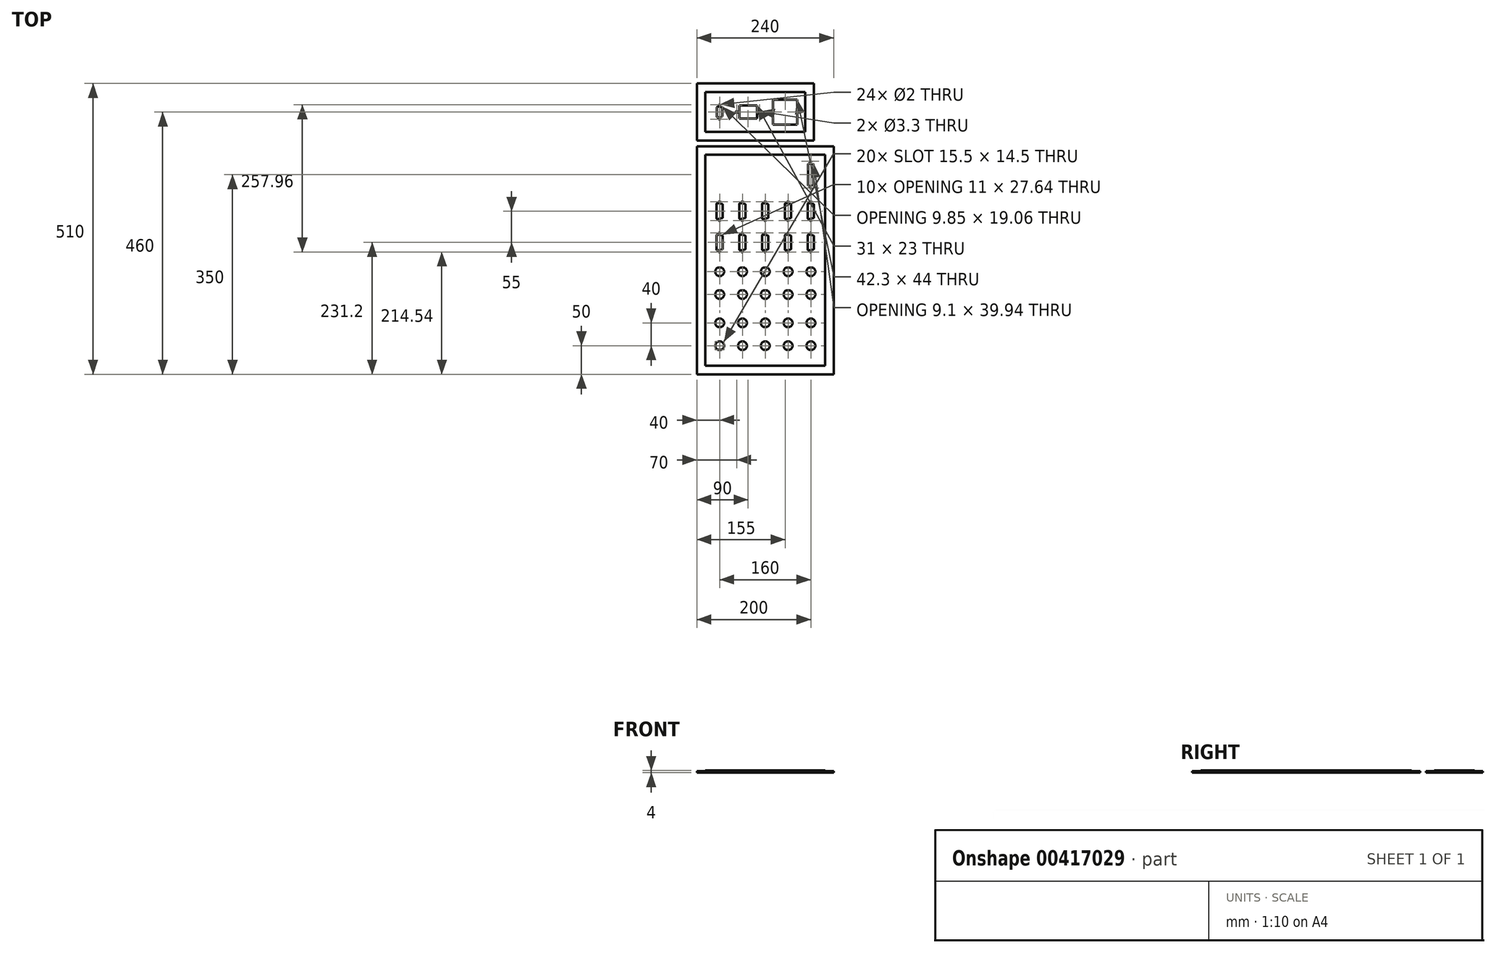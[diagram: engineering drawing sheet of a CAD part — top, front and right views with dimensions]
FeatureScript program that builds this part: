
annotation { "Feature Type Name" : "Feature", "Feature Type Description" : "" }
export const myFeature = defineFeature(function(context is Context, id is Id, definition is map)
    precondition{}
    {
        {
            var Q0;
            Q0=qCreatedBy(makeId("Top.planeOp"),FACE);
            var sketch = newSketch(context, id + "F0", { "sketchPlane" : qUnion([Q0])});
            skLineSegment(sketch, "E0.bottom", {"start": v(-120, -200) * mm, "end": v(120, -200) * mm});
            skLineSegment(sketch, "E0.top", {"start": v(-120, 200) * mm, "end": v(120, 200) * mm});
            skLineSegment(sketch, "E0.left", {"start": v(-120, -200) * mm, "end": v(-120, 200) * mm});
            skLineSegment(sketch, "E0.right", {"start": v(120, -200) * mm, "end": v(120, 200) * mm});
            skArc(sketch, "E1", {"start": v(-82.74, -102.75) * mm, "mid": v(-87.75, -110) * mm, "end": v(-82.74, -117.25) * mm});
            skLineSegment(sketch, "E2", {"start": v(-82.74, -102.75) * mm, "end": v(-77.26, -102.75) * mm});
            skLineSegment(sketch, "E3", {"start": v(-77.26, -117.25) * mm, "end": v(-82.74, -117.25) * mm});
            skLineSegment(sketch, "E4", {"start": v(-80, -110) * mm, "end": v(-87.75, -110) * mm, "construction": true});
            skArc(sketch, "E5.trimOffspring", {"start": v(-77.26, -117.25) * mm, "mid": v(-72.25, -110) * mm, "end": v(-77.26, -102.75) * mm});
            skLineSegment(sketch, "E6.0.1.0", {"start": v(-77.26, -157.25) * mm, "end": v(-82.74, -157.25) * mm});
            skLineSegment(sketch, "E6.0.1.1", {"start": v(-82.74, -142.75) * mm, "end": v(-77.26, -142.75) * mm});
            skArc(sketch, "E6.0.1.2", {"start": v(-82.74, -142.75) * mm, "mid": v(-87.75, -150) * mm, "end": v(-82.74, -157.25) * mm});
            skLineSegment(sketch, "E6.0.1.3", {"start": v(-80, -150) * mm, "end": v(-87.75, -150) * mm, "construction": true});
            skArc(sketch, "E6.0.1.4", {"start": v(-77.26, -157.25) * mm, "mid": v(-72.25, -150) * mm, "end": v(-77.26, -142.75) * mm});
            skLineSegment(sketch, "E6.direction1", {"start": v(-82.74, -117.25) * mm, "end": v(-42.74, -117.25) * mm, "construction": true});
            skLineSegment(sketch, "E6.direction2", {"start": v(-82.74, -117.25) * mm, "end": v(-82.74, -157.25) * mm, "construction": true});
            skLineSegment(sketch, "E7.0.1.0", {"start": v(-37.26, -117.25) * mm, "end": v(-42.74, -117.25) * mm});
            skLineSegment(sketch, "E7.3.1.0", {"start": v(-42.74, -102.75) * mm, "end": v(-37.26, -102.75) * mm});
            skArc(sketch, "E7.6.1.0", {"start": v(-42.74, -102.75) * mm, "mid": v(-47.75, -110) * mm, "end": v(-42.74, -117.25) * mm});
            skLineSegment(sketch, "E7.10.1.0", {"start": v(-40, -110) * mm, "end": v(-47.75, -110) * mm, "construction": true});
            skArc(sketch, "E7.13.1.0", {"start": v(-37.26, -117.25) * mm, "mid": v(-32.25, -110) * mm, "end": v(-37.26, -102.75) * mm});
            skLineSegment(sketch, "E7.0.1.1", {"start": v(-37.26, -157.25) * mm, "end": v(-42.74, -157.25) * mm});
            skLineSegment(sketch, "E7.3.1.1", {"start": v(-42.74, -142.75) * mm, "end": v(-37.26, -142.75) * mm});
            skArc(sketch, "E7.6.1.1", {"start": v(-42.74, -142.75) * mm, "mid": v(-47.75, -150) * mm, "end": v(-42.74, -157.25) * mm});
            skLineSegment(sketch, "E7.10.1.1", {"start": v(-40, -150) * mm, "end": v(-47.75, -150) * mm, "construction": true});
            skArc(sketch, "E7.13.1.1", {"start": v(-37.26, -157.25) * mm, "mid": v(-32.25, -150) * mm, "end": v(-37.26, -142.75) * mm});
            skLineSegment(sketch, "E7.0.2.0", {"start": v(2.74, -117.25) * mm, "end": v(-2.74, -117.25) * mm});
            skLineSegment(sketch, "E7.3.2.0", {"start": v(-2.74, -102.75) * mm, "end": v(2.74, -102.75) * mm});
            skArc(sketch, "E7.6.2.0", {"start": v(-2.74, -102.75) * mm, "mid": v(-7.75, -110) * mm, "end": v(-2.74, -117.25) * mm});
            skLineSegment(sketch, "E7.10.2.0", {"start": v(0, -110) * mm, "end": v(-7.75, -110) * mm, "construction": true});
            skArc(sketch, "E7.13.2.0", {"start": v(2.74, -117.25) * mm, "mid": v(7.75, -110) * mm, "end": v(2.74, -102.75) * mm});
            skLineSegment(sketch, "E7.0.2.1", {"start": v(2.74, -157.25) * mm, "end": v(-2.74, -157.25) * mm});
            skLineSegment(sketch, "E7.3.2.1", {"start": v(-2.74, -142.75) * mm, "end": v(2.74, -142.75) * mm});
            skArc(sketch, "E7.6.2.1", {"start": v(-2.74, -142.75) * mm, "mid": v(-7.75, -150) * mm, "end": v(-2.74, -157.25) * mm});
            skLineSegment(sketch, "E7.10.2.1", {"start": v(0, -150) * mm, "end": v(-7.75, -150) * mm, "construction": true});
            skArc(sketch, "E7.13.2.1", {"start": v(2.74, -157.25) * mm, "mid": v(7.75, -150) * mm, "end": v(2.74, -142.75) * mm});
            skLineSegment(sketch, "E7.0.3.0", {"start": v(42.74, -117.25) * mm, "end": v(37.26, -117.25) * mm});
            skLineSegment(sketch, "E7.3.3.0", {"start": v(37.26, -102.75) * mm, "end": v(42.74, -102.75) * mm});
            skArc(sketch, "E7.6.3.0", {"start": v(37.26, -102.75) * mm, "mid": v(32.25, -110) * mm, "end": v(37.26, -117.25) * mm});
            skLineSegment(sketch, "E7.10.3.0", {"start": v(40, -110) * mm, "end": v(32.25, -110) * mm, "construction": true});
            skArc(sketch, "E7.13.3.0", {"start": v(42.74, -117.25) * mm, "mid": v(47.75, -110) * mm, "end": v(42.74, -102.75) * mm});
            skLineSegment(sketch, "E7.0.3.1", {"start": v(42.74, -157.25) * mm, "end": v(37.26, -157.25) * mm});
            skLineSegment(sketch, "E7.3.3.1", {"start": v(37.26, -142.75) * mm, "end": v(42.74, -142.75) * mm});
            skArc(sketch, "E7.6.3.1", {"start": v(37.26, -142.75) * mm, "mid": v(32.25, -150) * mm, "end": v(37.26, -157.25) * mm});
            skLineSegment(sketch, "E7.10.3.1", {"start": v(40, -150) * mm, "end": v(32.25, -150) * mm, "construction": true});
            skArc(sketch, "E7.13.3.1", {"start": v(42.74, -157.25) * mm, "mid": v(47.75, -150) * mm, "end": v(42.74, -142.75) * mm});
            skLineSegment(sketch, "E7.0.4.0", {"start": v(82.74, -117.25) * mm, "end": v(77.26, -117.25) * mm});
            skLineSegment(sketch, "E7.3.4.0", {"start": v(77.26, -102.75) * mm, "end": v(82.74, -102.75) * mm});
            skArc(sketch, "E7.6.4.0", {"start": v(77.26, -102.75) * mm, "mid": v(72.25, -110) * mm, "end": v(77.26, -117.25) * mm});
            skLineSegment(sketch, "E7.10.4.0", {"start": v(80, -110) * mm, "end": v(72.25, -110) * mm, "construction": true});
            skArc(sketch, "E7.13.4.0", {"start": v(82.74, -117.25) * mm, "mid": v(87.75, -110) * mm, "end": v(82.74, -102.75) * mm});
            skLineSegment(sketch, "E7.0.4.1", {"start": v(82.74, -157.25) * mm, "end": v(77.26, -157.25) * mm});
            skLineSegment(sketch, "E7.3.4.1", {"start": v(77.26, -142.75) * mm, "end": v(82.74, -142.75) * mm});
            skArc(sketch, "E7.6.4.1", {"start": v(77.26, -142.75) * mm, "mid": v(72.25, -150) * mm, "end": v(77.26, -157.25) * mm});
            skLineSegment(sketch, "E7.10.4.1", {"start": v(80, -150) * mm, "end": v(72.25, -150) * mm, "construction": true});
            skArc(sketch, "E7.13.4.1", {"start": v(82.74, -157.25) * mm, "mid": v(87.75, -150) * mm, "end": v(82.74, -142.75) * mm});
            skLineSegment(sketch, "E8.bottom", {"start": v(-105, 185) * mm, "end": v(105, 185) * mm, "construction": true});
            skLineSegment(sketch, "E8.top", {"start": v(-105, -185) * mm, "end": v(105, -185) * mm, "construction": true});
            skLineSegment(sketch, "E8.left", {"start": v(-105, 185) * mm, "end": v(-105, -185) * mm, "construction": true});
            skLineSegment(sketch, "E8.right", {"start": v(105, 185) * mm, "end": v(105, -185) * mm, "construction": true});
            skArc(sketch, "E9", {"start": v(-82.74, -12.75) * mm, "mid": v(-87.75, -20) * mm, "end": v(-82.74, -27.25) * mm});
            skLineSegment(sketch, "E10", {"start": v(-82.74, -12.75) * mm, "end": v(-77.26, -12.75) * mm});
            skLineSegment(sketch, "E11", {"start": v(-77.26, -27.25) * mm, "end": v(-82.74, -27.25) * mm});
            skLineSegment(sketch, "E12", {"start": v(-80, -20) * mm, "end": v(-87.75, -20) * mm, "construction": true});
            skArc(sketch, "E13.trimOffspring", {"start": v(-77.26, -27.25) * mm, "mid": v(-72.25, -20) * mm, "end": v(-77.26, -12.75) * mm});
            skLineSegment(sketch, "E14", {"start": v(-83.74, 100) * mm, "end": v(-75.74, 98.59) * mm});
            skLineSegment(sketch, "E15", {"start": v(-74.5, 97.11) * mm, "end": v(-74.5, 75.29) * mm});
            skLineSegment(sketch, "E16", {"start": v(-75.74, 73.81) * mm, "end": v(-83.74, 72.4) * mm});
            skLineSegment(sketch, "E17", {"start": v(-85.5, 73.88) * mm, "end": v(-85.5, 98.52) * mm});
            skLineSegment(sketch, "E18", {"start": v(-80, 99.34) * mm, "end": v(-80, 73.06) * mm, "construction": true});
            skPoint(sketch, "E19.visualSharp", {"position": v(-85.5, 100.31) * mm});
            skArc(sketch, "E19.filletArc", {"start": v(-83.74, 100) * mm, "mid": v(-84.96, 99.67) * mm, "end": v(-85.5, 98.52) * mm});
            skPoint(sketch, "E20.visualSharp", {"position": v(-74.5, 98.37) * mm});
            skArc(sketch, "E20.filletArc", {"start": v(-74.5, 97.11) * mm, "mid": v(-74.85, 98.08) * mm, "end": v(-75.74, 98.59) * mm});
            skPoint(sketch, "E21.visualSharp", {"position": v(-74.5, 74.03) * mm});
            skArc(sketch, "E21.filletArc", {"start": v(-75.74, 73.81) * mm, "mid": v(-74.85, 74.32) * mm, "end": v(-74.5, 75.29) * mm});
            skPoint(sketch, "E22.visualSharp", {"position": v(-85.5, 72.09) * mm});
            skArc(sketch, "E22.filletArc", {"start": v(-85.5, 73.88) * mm, "mid": v(-84.96, 72.73) * mm, "end": v(-83.74, 72.4) * mm});
            skCircle(sketch, "E23", {"center": v(-80, 102.86) * mm, "radius": 1 * mm});
            skCircle(sketch, "E24", {"center": v(-80, 69.54) * mm, "radius": 1 * mm});
            skLineSegment(sketch, "E25", {"start": v(-84, 86.2) * mm, "end": v(-76.01, 86.2) * mm, "construction": true});
            skPoint(sketch, "E26.0.1.0", {"position": v(-85.5, 45.31) * mm});
            skPoint(sketch, "E26.0.1.1", {"position": v(-85.5, 17.09) * mm});
            skPoint(sketch, "E26.0.1.2", {"position": v(-74.5, 43.37) * mm});
            skLineSegment(sketch, "E26.0.1.3", {"start": v(-80, 44.34) * mm, "end": v(-80, 18.06) * mm, "construction": true});
            skLineSegment(sketch, "E26.0.1.4", {"start": v(-84, 31.2) * mm, "end": v(-76.01, 31.2) * mm, "construction": true});
            skPoint(sketch, "E26.0.1.5", {"position": v(-74.5, 19.03) * mm});
            skLineSegment(sketch, "E26.0.1.6", {"start": v(-74.5, 42.11) * mm, "end": v(-74.5, 20.29) * mm});
            skLineSegment(sketch, "E26.0.1.7", {"start": v(-85.5, 18.88) * mm, "end": v(-85.5, 43.52) * mm});
            skCircle(sketch, "E26.0.1.8", {"center": v(-80, 47.86) * mm, "radius": 1 * mm});
            skLineSegment(sketch, "E26.0.1.9", {"start": v(-83.74, 45) * mm, "end": v(-75.74, 43.59) * mm});
            skCircle(sketch, "E26.0.1.10", {"center": v(-80, 14.54) * mm, "radius": 1 * mm});
            skArc(sketch, "E26.0.1.11", {"start": v(-83.74, 45) * mm, "mid": v(-84.96, 44.67) * mm, "end": v(-85.5, 43.52) * mm});
            skArc(sketch, "E26.0.1.12", {"start": v(-85.5, 18.88) * mm, "mid": v(-84.96, 17.73) * mm, "end": v(-83.74, 17.4) * mm});
            skLineSegment(sketch, "E26.0.1.13", {"start": v(-75.74, 18.81) * mm, "end": v(-83.74, 17.4) * mm});
            skArc(sketch, "E26.0.1.14", {"start": v(-75.74, 18.81) * mm, "mid": v(-74.85, 19.32) * mm, "end": v(-74.5, 20.29) * mm});
            skArc(sketch, "E26.0.1.15", {"start": v(-74.5, 42.11) * mm, "mid": v(-74.85, 43.08) * mm, "end": v(-75.74, 43.59) * mm});
            skPoint(sketch, "E26.1.0.0", {"position": v(-45.5, 100.31) * mm});
            skPoint(sketch, "E26.1.0.1", {"position": v(-45.5, 72.09) * mm});
            skPoint(sketch, "E26.1.0.2", {"position": v(-34.5, 98.37) * mm});
            skLineSegment(sketch, "E26.1.0.3", {"start": v(-40, 99.34) * mm, "end": v(-40, 73.06) * mm, "construction": true});
            skLineSegment(sketch, "E26.1.0.4", {"start": v(-44, 86.2) * mm, "end": v(-36.01, 86.2) * mm, "construction": true});
            skPoint(sketch, "E26.1.0.5", {"position": v(-34.5, 74.03) * mm});
            skLineSegment(sketch, "E26.1.0.6", {"start": v(-34.5, 97.11) * mm, "end": v(-34.5, 75.29) * mm});
            skLineSegment(sketch, "E26.1.0.7", {"start": v(-45.5, 73.88) * mm, "end": v(-45.5, 98.52) * mm});
            skCircle(sketch, "E26.1.0.8", {"center": v(-40, 102.86) * mm, "radius": 1 * mm});
            skLineSegment(sketch, "E26.1.0.9", {"start": v(-43.74, 100) * mm, "end": v(-35.74, 98.59) * mm});
            skCircle(sketch, "E26.1.0.10", {"center": v(-40, 69.54) * mm, "radius": 1 * mm});
            skArc(sketch, "E26.1.0.11", {"start": v(-43.74, 100) * mm, "mid": v(-44.96, 99.67) * mm, "end": v(-45.5, 98.52) * mm});
            skArc(sketch, "E26.1.0.12", {"start": v(-45.5, 73.88) * mm, "mid": v(-44.96, 72.73) * mm, "end": v(-43.74, 72.4) * mm});
            skLineSegment(sketch, "E26.1.0.13", {"start": v(-35.74, 73.81) * mm, "end": v(-43.74, 72.4) * mm});
            skArc(sketch, "E26.1.0.14", {"start": v(-35.74, 73.81) * mm, "mid": v(-34.85, 74.32) * mm, "end": v(-34.5, 75.29) * mm});
            skArc(sketch, "E26.1.0.15", {"start": v(-34.5, 97.11) * mm, "mid": v(-34.85, 98.08) * mm, "end": v(-35.74, 98.59) * mm});
            skPoint(sketch, "E26.1.1.0", {"position": v(-45.5, 45.31) * mm});
            skPoint(sketch, "E26.1.1.1", {"position": v(-45.5, 17.09) * mm});
            skPoint(sketch, "E26.1.1.2", {"position": v(-34.5, 43.37) * mm});
            skLineSegment(sketch, "E26.1.1.3", {"start": v(-40, 44.34) * mm, "end": v(-40, 18.06) * mm, "construction": true});
            skLineSegment(sketch, "E26.1.1.4", {"start": v(-44, 31.2) * mm, "end": v(-36.01, 31.2) * mm, "construction": true});
            skPoint(sketch, "E26.1.1.5", {"position": v(-34.5, 19.03) * mm});
            skLineSegment(sketch, "E26.1.1.6", {"start": v(-34.5, 42.11) * mm, "end": v(-34.5, 20.29) * mm});
            skLineSegment(sketch, "E26.1.1.7", {"start": v(-45.5, 18.88) * mm, "end": v(-45.5, 43.52) * mm});
            skCircle(sketch, "E26.1.1.8", {"center": v(-40, 47.86) * mm, "radius": 1 * mm});
            skLineSegment(sketch, "E26.1.1.9", {"start": v(-43.74, 45) * mm, "end": v(-35.74, 43.59) * mm});
            skCircle(sketch, "E26.1.1.10", {"center": v(-40, 14.54) * mm, "radius": 1 * mm});
            skArc(sketch, "E26.1.1.11", {"start": v(-43.74, 45) * mm, "mid": v(-44.96, 44.67) * mm, "end": v(-45.5, 43.52) * mm});
            skArc(sketch, "E26.1.1.12", {"start": v(-45.5, 18.88) * mm, "mid": v(-44.96, 17.73) * mm, "end": v(-43.74, 17.4) * mm});
            skLineSegment(sketch, "E26.1.1.13", {"start": v(-35.74, 18.81) * mm, "end": v(-43.74, 17.4) * mm});
            skArc(sketch, "E26.1.1.14", {"start": v(-35.74, 18.81) * mm, "mid": v(-34.85, 19.32) * mm, "end": v(-34.5, 20.29) * mm});
            skArc(sketch, "E26.1.1.15", {"start": v(-34.5, 42.11) * mm, "mid": v(-34.85, 43.08) * mm, "end": v(-35.74, 43.59) * mm});
            skPoint(sketch, "E26.2.0.0", {"position": v(-5.5, 100.31) * mm});
            skPoint(sketch, "E26.2.0.1", {"position": v(-5.5, 72.09) * mm});
            skPoint(sketch, "E26.2.0.2", {"position": v(5.5, 98.37) * mm});
            skLineSegment(sketch, "E26.2.0.3", {"start": v(0, 99.34) * mm, "end": v(0, 73.06) * mm, "construction": true});
            skLineSegment(sketch, "E26.2.0.4", {"start": v(-4, 86.2) * mm, "end": v(3.99, 86.2) * mm, "construction": true});
            skPoint(sketch, "E26.2.0.5", {"position": v(5.5, 74.03) * mm});
            skLineSegment(sketch, "E26.2.0.6", {"start": v(5.5, 97.11) * mm, "end": v(5.5, 75.29) * mm});
            skLineSegment(sketch, "E26.2.0.7", {"start": v(-5.5, 73.88) * mm, "end": v(-5.5, 98.52) * mm});
            skCircle(sketch, "E26.2.0.8", {"center": v(0, 102.86) * mm, "radius": 1 * mm});
            skLineSegment(sketch, "E26.2.0.9", {"start": v(-3.74, 100) * mm, "end": v(4.26, 98.59) * mm});
            skCircle(sketch, "E26.2.0.10", {"center": v(0, 69.54) * mm, "radius": 1 * mm});
            skArc(sketch, "E26.2.0.11", {"start": v(-3.74, 100) * mm, "mid": v(-4.96, 99.67) * mm, "end": v(-5.5, 98.52) * mm});
            skArc(sketch, "E26.2.0.12", {"start": v(-5.5, 73.88) * mm, "mid": v(-4.96, 72.73) * mm, "end": v(-3.74, 72.4) * mm});
            skLineSegment(sketch, "E26.2.0.13", {"start": v(4.26, 73.81) * mm, "end": v(-3.74, 72.4) * mm});
            skArc(sketch, "E26.2.0.14", {"start": v(4.26, 73.81) * mm, "mid": v(5.15, 74.32) * mm, "end": v(5.5, 75.29) * mm});
            skArc(sketch, "E26.2.0.15", {"start": v(5.5, 97.11) * mm, "mid": v(5.15, 98.08) * mm, "end": v(4.26, 98.59) * mm});
            skPoint(sketch, "E26.2.1.0", {"position": v(-5.5, 45.31) * mm});
            skPoint(sketch, "E26.2.1.1", {"position": v(-5.5, 17.09) * mm});
            skPoint(sketch, "E26.2.1.2", {"position": v(5.5, 43.37) * mm});
            skLineSegment(sketch, "E26.2.1.3", {"start": v(0, 44.34) * mm, "end": v(0, 18.06) * mm, "construction": true});
            skLineSegment(sketch, "E26.2.1.4", {"start": v(-4, 31.2) * mm, "end": v(3.99, 31.2) * mm, "construction": true});
            skPoint(sketch, "E26.2.1.5", {"position": v(5.5, 19.03) * mm});
            skLineSegment(sketch, "E26.2.1.6", {"start": v(5.5, 42.11) * mm, "end": v(5.5, 20.29) * mm});
            skLineSegment(sketch, "E26.2.1.7", {"start": v(-5.5, 18.88) * mm, "end": v(-5.5, 43.52) * mm});
            skCircle(sketch, "E26.2.1.8", {"center": v(0, 47.86) * mm, "radius": 1 * mm});
            skLineSegment(sketch, "E26.2.1.9", {"start": v(-3.74, 45) * mm, "end": v(4.26, 43.59) * mm});
            skCircle(sketch, "E26.2.1.10", {"center": v(0, 14.54) * mm, "radius": 1 * mm});
            skArc(sketch, "E26.2.1.11", {"start": v(-3.74, 45) * mm, "mid": v(-4.96, 44.67) * mm, "end": v(-5.5, 43.52) * mm});
            skArc(sketch, "E26.2.1.12", {"start": v(-5.5, 18.88) * mm, "mid": v(-4.96, 17.73) * mm, "end": v(-3.74, 17.4) * mm});
            skLineSegment(sketch, "E26.2.1.13", {"start": v(4.26, 18.81) * mm, "end": v(-3.74, 17.4) * mm});
            skArc(sketch, "E26.2.1.14", {"start": v(4.26, 18.81) * mm, "mid": v(5.15, 19.32) * mm, "end": v(5.5, 20.29) * mm});
            skArc(sketch, "E26.2.1.15", {"start": v(5.5, 42.11) * mm, "mid": v(5.15, 43.08) * mm, "end": v(4.26, 43.59) * mm});
            skPoint(sketch, "E26.3.0.0", {"position": v(34.5, 100.31) * mm});
            skPoint(sketch, "E26.3.0.1", {"position": v(34.5, 72.09) * mm});
            skPoint(sketch, "E26.3.0.2", {"position": v(45.5, 98.37) * mm});
            skLineSegment(sketch, "E26.3.0.3", {"start": v(40, 99.34) * mm, "end": v(40, 73.06) * mm, "construction": true});
            skLineSegment(sketch, "E26.3.0.4", {"start": v(36, 86.2) * mm, "end": v(43.99, 86.2) * mm, "construction": true});
            skPoint(sketch, "E26.3.0.5", {"position": v(45.5, 74.03) * mm});
            skLineSegment(sketch, "E26.3.0.6", {"start": v(45.5, 97.11) * mm, "end": v(45.5, 75.29) * mm});
            skLineSegment(sketch, "E26.3.0.7", {"start": v(34.5, 73.88) * mm, "end": v(34.5, 98.52) * mm});
            skCircle(sketch, "E26.3.0.8", {"center": v(40, 102.86) * mm, "radius": 1 * mm});
            skLineSegment(sketch, "E26.3.0.9", {"start": v(36.26, 100) * mm, "end": v(44.26, 98.59) * mm});
            skCircle(sketch, "E26.3.0.10", {"center": v(40, 69.54) * mm, "radius": 1 * mm});
            skArc(sketch, "E26.3.0.11", {"start": v(36.26, 100) * mm, "mid": v(35.04, 99.67) * mm, "end": v(34.5, 98.52) * mm});
            skArc(sketch, "E26.3.0.12", {"start": v(34.5, 73.88) * mm, "mid": v(35.04, 72.73) * mm, "end": v(36.26, 72.4) * mm});
            skLineSegment(sketch, "E26.3.0.13", {"start": v(44.26, 73.81) * mm, "end": v(36.26, 72.4) * mm});
            skArc(sketch, "E26.3.0.14", {"start": v(44.26, 73.81) * mm, "mid": v(45.15, 74.32) * mm, "end": v(45.5, 75.29) * mm});
            skArc(sketch, "E26.3.0.15", {"start": v(45.5, 97.11) * mm, "mid": v(45.15, 98.08) * mm, "end": v(44.26, 98.59) * mm});
            skPoint(sketch, "E26.3.1.0", {"position": v(34.5, 45.31) * mm});
            skPoint(sketch, "E26.3.1.1", {"position": v(34.5, 17.09) * mm});
            skPoint(sketch, "E26.3.1.2", {"position": v(45.5, 43.37) * mm});
            skLineSegment(sketch, "E26.3.1.3", {"start": v(40, 44.34) * mm, "end": v(40, 18.06) * mm, "construction": true});
            skLineSegment(sketch, "E26.3.1.4", {"start": v(36, 31.2) * mm, "end": v(43.99, 31.2) * mm, "construction": true});
            skPoint(sketch, "E26.3.1.5", {"position": v(45.5, 19.03) * mm});
            skLineSegment(sketch, "E26.3.1.6", {"start": v(45.5, 42.11) * mm, "end": v(45.5, 20.29) * mm});
            skLineSegment(sketch, "E26.3.1.7", {"start": v(34.5, 18.88) * mm, "end": v(34.5, 43.52) * mm});
            skCircle(sketch, "E26.3.1.8", {"center": v(40, 47.86) * mm, "radius": 1 * mm});
            skLineSegment(sketch, "E26.3.1.9", {"start": v(36.26, 45) * mm, "end": v(44.26, 43.59) * mm});
            skCircle(sketch, "E26.3.1.10", {"center": v(40, 14.54) * mm, "radius": 1 * mm});
            skArc(sketch, "E26.3.1.11", {"start": v(36.26, 45) * mm, "mid": v(35.04, 44.67) * mm, "end": v(34.5, 43.52) * mm});
            skArc(sketch, "E26.3.1.12", {"start": v(34.5, 18.88) * mm, "mid": v(35.04, 17.73) * mm, "end": v(36.26, 17.4) * mm});
            skLineSegment(sketch, "E26.3.1.13", {"start": v(44.26, 18.81) * mm, "end": v(36.26, 17.4) * mm});
            skArc(sketch, "E26.3.1.14", {"start": v(44.26, 18.81) * mm, "mid": v(45.15, 19.32) * mm, "end": v(45.5, 20.29) * mm});
            skArc(sketch, "E26.3.1.15", {"start": v(45.5, 42.11) * mm, "mid": v(45.15, 43.08) * mm, "end": v(44.26, 43.59) * mm});
            skPoint(sketch, "E26.4.0.0", {"position": v(74.5, 100.31) * mm});
            skPoint(sketch, "E26.4.0.1", {"position": v(74.5, 72.09) * mm});
            skPoint(sketch, "E26.4.0.2", {"position": v(85.5, 98.37) * mm});
            skLineSegment(sketch, "E26.4.0.3", {"start": v(80, 99.34) * mm, "end": v(80, 73.06) * mm, "construction": true});
            skLineSegment(sketch, "E26.4.0.4", {"start": v(76, 86.2) * mm, "end": v(83.99, 86.2) * mm, "construction": true});
            skPoint(sketch, "E26.4.0.5", {"position": v(85.5, 74.03) * mm});
            skLineSegment(sketch, "E26.4.0.6", {"start": v(85.5, 97.11) * mm, "end": v(85.5, 75.29) * mm});
            skLineSegment(sketch, "E26.4.0.7", {"start": v(74.5, 73.88) * mm, "end": v(74.5, 98.52) * mm});
            skCircle(sketch, "E26.4.0.8", {"center": v(80, 102.86) * mm, "radius": 1 * mm});
            skLineSegment(sketch, "E26.4.0.9", {"start": v(76.26, 100) * mm, "end": v(84.26, 98.59) * mm});
            skCircle(sketch, "E26.4.0.10", {"center": v(80, 69.54) * mm, "radius": 1 * mm});
            skArc(sketch, "E26.4.0.11", {"start": v(76.26, 100) * mm, "mid": v(75.04, 99.67) * mm, "end": v(74.5, 98.52) * mm});
            skArc(sketch, "E26.4.0.12", {"start": v(74.5, 73.88) * mm, "mid": v(75.04, 72.73) * mm, "end": v(76.26, 72.4) * mm});
            skLineSegment(sketch, "E26.4.0.13", {"start": v(84.26, 73.81) * mm, "end": v(76.26, 72.4) * mm});
            skArc(sketch, "E26.4.0.14", {"start": v(84.26, 73.81) * mm, "mid": v(85.15, 74.32) * mm, "end": v(85.5, 75.29) * mm});
            skArc(sketch, "E26.4.0.15", {"start": v(85.5, 97.11) * mm, "mid": v(85.15, 98.08) * mm, "end": v(84.26, 98.59) * mm});
            skPoint(sketch, "E26.4.1.0", {"position": v(74.5, 45.31) * mm});
            skPoint(sketch, "E26.4.1.1", {"position": v(74.5, 17.09) * mm});
            skPoint(sketch, "E26.4.1.2", {"position": v(85.5, 43.37) * mm});
            skLineSegment(sketch, "E26.4.1.3", {"start": v(80, 44.34) * mm, "end": v(80, 18.06) * mm, "construction": true});
            skLineSegment(sketch, "E26.4.1.4", {"start": v(76, 31.2) * mm, "end": v(83.99, 31.2) * mm, "construction": true});
            skPoint(sketch, "E26.4.1.5", {"position": v(85.5, 19.03) * mm});
            skLineSegment(sketch, "E26.4.1.6", {"start": v(85.5, 42.11) * mm, "end": v(85.5, 20.29) * mm});
            skLineSegment(sketch, "E26.4.1.7", {"start": v(74.5, 18.88) * mm, "end": v(74.5, 43.52) * mm});
            skCircle(sketch, "E26.4.1.8", {"center": v(80, 47.86) * mm, "radius": 1 * mm});
            skLineSegment(sketch, "E26.4.1.9", {"start": v(76.26, 45) * mm, "end": v(84.26, 43.59) * mm});
            skCircle(sketch, "E26.4.1.10", {"center": v(80, 14.54) * mm, "radius": 1 * mm});
            skArc(sketch, "E26.4.1.11", {"start": v(76.26, 45) * mm, "mid": v(75.04, 44.67) * mm, "end": v(74.5, 43.52) * mm});
            skArc(sketch, "E26.4.1.12", {"start": v(74.5, 18.88) * mm, "mid": v(75.04, 17.73) * mm, "end": v(76.26, 17.4) * mm});
            skLineSegment(sketch, "E26.4.1.13", {"start": v(84.26, 18.81) * mm, "end": v(76.26, 17.4) * mm});
            skArc(sketch, "E26.4.1.14", {"start": v(84.26, 18.81) * mm, "mid": v(85.15, 19.32) * mm, "end": v(85.5, 20.29) * mm});
            skArc(sketch, "E26.4.1.15", {"start": v(85.5, 42.11) * mm, "mid": v(85.15, 43.08) * mm, "end": v(84.26, 43.59) * mm});
            skLineSegment(sketch, "E26.direction1", {"start": v(-85.5, 72.09) * mm, "end": v(-45.5, 72.09) * mm, "construction": true});
            skLineSegment(sketch, "E26.direction2", {"start": v(-85.5, 72.09) * mm, "end": v(-85.5, 17.09) * mm, "construction": true});
            skLineSegment(sketch, "E27.0.1.0", {"start": v(-80, -60) * mm, "end": v(-87.75, -60) * mm, "construction": true});
            skArc(sketch, "E27.0.1.1", {"start": v(-77.26, -67.25) * mm, "mid": v(-72.25, -60) * mm, "end": v(-77.26, -52.75) * mm});
            skArc(sketch, "E27.0.1.2", {"start": v(-82.74, -52.75) * mm, "mid": v(-87.75, -60) * mm, "end": v(-82.74, -67.25) * mm});
            skLineSegment(sketch, "E27.0.1.3", {"start": v(-82.74, -52.75) * mm, "end": v(-77.26, -52.75) * mm});
            skLineSegment(sketch, "E27.0.1.4", {"start": v(-77.26, -67.25) * mm, "end": v(-82.74, -67.25) * mm});
            skLineSegment(sketch, "E27.1.0.0", {"start": v(-40, -20) * mm, "end": v(-47.75, -20) * mm, "construction": true});
            skArc(sketch, "E27.1.0.1", {"start": v(-37.26, -27.25) * mm, "mid": v(-32.25, -20) * mm, "end": v(-37.26, -12.75) * mm});
            skArc(sketch, "E27.1.0.2", {"start": v(-42.74, -12.75) * mm, "mid": v(-47.75, -20) * mm, "end": v(-42.74, -27.25) * mm});
            skLineSegment(sketch, "E27.1.0.3", {"start": v(-42.74, -12.75) * mm, "end": v(-37.26, -12.75) * mm});
            skLineSegment(sketch, "E27.1.0.4", {"start": v(-37.26, -27.25) * mm, "end": v(-42.74, -27.25) * mm});
            skLineSegment(sketch, "E27.1.1.0", {"start": v(-40, -60) * mm, "end": v(-47.75, -60) * mm, "construction": true});
            skArc(sketch, "E27.1.1.1", {"start": v(-37.26, -67.25) * mm, "mid": v(-32.25, -60) * mm, "end": v(-37.26, -52.75) * mm});
            skArc(sketch, "E27.1.1.2", {"start": v(-42.74, -52.75) * mm, "mid": v(-47.75, -60) * mm, "end": v(-42.74, -67.25) * mm});
            skLineSegment(sketch, "E27.1.1.3", {"start": v(-42.74, -52.75) * mm, "end": v(-37.26, -52.75) * mm});
            skLineSegment(sketch, "E27.1.1.4", {"start": v(-37.26, -67.25) * mm, "end": v(-42.74, -67.25) * mm});
            skLineSegment(sketch, "E27.2.0.0", {"start": v(0, -20) * mm, "end": v(-7.75, -20) * mm, "construction": true});
            skArc(sketch, "E27.2.0.1", {"start": v(2.74, -27.25) * mm, "mid": v(7.75, -20) * mm, "end": v(2.74, -12.75) * mm});
            skArc(sketch, "E27.2.0.2", {"start": v(-2.74, -12.75) * mm, "mid": v(-7.75, -20) * mm, "end": v(-2.74, -27.25) * mm});
            skLineSegment(sketch, "E27.2.0.3", {"start": v(-2.74, -12.75) * mm, "end": v(2.74, -12.75) * mm});
            skLineSegment(sketch, "E27.2.0.4", {"start": v(2.74, -27.25) * mm, "end": v(-2.74, -27.25) * mm});
            skLineSegment(sketch, "E27.2.1.0", {"start": v(0, -60) * mm, "end": v(-7.75, -60) * mm, "construction": true});
            skArc(sketch, "E27.2.1.1", {"start": v(2.74, -67.25) * mm, "mid": v(7.75, -60) * mm, "end": v(2.74, -52.75) * mm});
            skArc(sketch, "E27.2.1.2", {"start": v(-2.74, -52.75) * mm, "mid": v(-7.75, -60) * mm, "end": v(-2.74, -67.25) * mm});
            skLineSegment(sketch, "E27.2.1.3", {"start": v(-2.74, -52.75) * mm, "end": v(2.74, -52.75) * mm});
            skLineSegment(sketch, "E27.2.1.4", {"start": v(2.74, -67.25) * mm, "end": v(-2.74, -67.25) * mm});
            skLineSegment(sketch, "E27.3.0.0", {"start": v(40, -20) * mm, "end": v(32.25, -20) * mm, "construction": true});
            skArc(sketch, "E27.3.0.1", {"start": v(42.74, -27.25) * mm, "mid": v(47.75, -20) * mm, "end": v(42.74, -12.75) * mm});
            skArc(sketch, "E27.3.0.2", {"start": v(37.26, -12.75) * mm, "mid": v(32.25, -20) * mm, "end": v(37.26, -27.25) * mm});
            skLineSegment(sketch, "E27.3.0.3", {"start": v(37.26, -12.75) * mm, "end": v(42.74, -12.75) * mm});
            skLineSegment(sketch, "E27.3.0.4", {"start": v(42.74, -27.25) * mm, "end": v(37.26, -27.25) * mm});
            skLineSegment(sketch, "E27.3.1.0", {"start": v(40, -60) * mm, "end": v(32.25, -60) * mm, "construction": true});
            skArc(sketch, "E27.3.1.1", {"start": v(42.74, -67.25) * mm, "mid": v(47.75, -60) * mm, "end": v(42.74, -52.75) * mm});
            skArc(sketch, "E27.3.1.2", {"start": v(37.26, -52.75) * mm, "mid": v(32.25, -60) * mm, "end": v(37.26, -67.25) * mm});
            skLineSegment(sketch, "E27.3.1.3", {"start": v(37.26, -52.75) * mm, "end": v(42.74, -52.75) * mm});
            skLineSegment(sketch, "E27.3.1.4", {"start": v(42.74, -67.25) * mm, "end": v(37.26, -67.25) * mm});
            skLineSegment(sketch, "E27.4.0.0", {"start": v(80, -20) * mm, "end": v(72.25, -20) * mm, "construction": true});
            skArc(sketch, "E27.4.0.1", {"start": v(82.74, -27.25) * mm, "mid": v(87.75, -20) * mm, "end": v(82.74, -12.75) * mm});
            skArc(sketch, "E27.4.0.2", {"start": v(77.26, -12.75) * mm, "mid": v(72.25, -20) * mm, "end": v(77.26, -27.25) * mm});
            skLineSegment(sketch, "E27.4.0.3", {"start": v(77.26, -12.75) * mm, "end": v(82.74, -12.75) * mm});
            skLineSegment(sketch, "E27.4.0.4", {"start": v(82.74, -27.25) * mm, "end": v(77.26, -27.25) * mm});
            skLineSegment(sketch, "E27.4.1.0", {"start": v(80, -60) * mm, "end": v(72.25, -60) * mm, "construction": true});
            skArc(sketch, "E27.4.1.1", {"start": v(82.74, -67.25) * mm, "mid": v(87.75, -60) * mm, "end": v(82.74, -52.75) * mm});
            skArc(sketch, "E27.4.1.2", {"start": v(77.26, -52.75) * mm, "mid": v(72.25, -60) * mm, "end": v(77.26, -67.25) * mm});
            skLineSegment(sketch, "E27.4.1.3", {"start": v(77.26, -52.75) * mm, "end": v(82.74, -52.75) * mm});
            skLineSegment(sketch, "E27.4.1.4", {"start": v(82.74, -67.25) * mm, "end": v(77.26, -67.25) * mm});
            skLineSegment(sketch, "E27.direction1", {"start": v(-82.74, -27.25) * mm, "end": v(-42.74, -27.25) * mm, "construction": true});
            skLineSegment(sketch, "E27.direction2", {"start": v(-82.74, -27.25) * mm, "end": v(-82.74, -67.25) * mm, "construction": true});
            skLineSegment(sketch, "E28", {"start": v(77.21, 169.95) * mm, "end": v(83.31, 168.87) * mm});
            skLineSegment(sketch, "E29", {"start": v(84.55, 167.4) * mm, "end": v(84.55, 132.6) * mm});
            skLineSegment(sketch, "E30", {"start": v(83.31, 131.13) * mm, "end": v(77.21, 130.05) * mm});
            skLineSegment(sketch, "E31", {"start": v(75.45, 131.53) * mm, "end": v(75.45, 168.47) * mm});
            skLineSegment(sketch, "E32", {"start": v(80, 169.46) * mm, "end": v(80, 130.54) * mm, "construction": true});
            skPoint(sketch, "E33.visualSharp", {"position": v(75.45, 170.26) * mm});
            skArc(sketch, "E33.filletArc", {"start": v(77.21, 169.95) * mm, "mid": v(75.99, 169.62) * mm, "end": v(75.45, 168.47) * mm});
            skPoint(sketch, "E34.visualSharp", {"position": v(84.55, 168.66) * mm});
            skArc(sketch, "E34.filletArc", {"start": v(84.55, 167.4) * mm, "mid": v(84.2, 168.36) * mm, "end": v(83.31, 168.87) * mm});
            skPoint(sketch, "E35.visualSharp", {"position": v(84.55, 131.34) * mm});
            skArc(sketch, "E35.filletArc", {"start": v(83.31, 131.13) * mm, "mid": v(84.2, 131.64) * mm, "end": v(84.55, 132.6) * mm});
            skPoint(sketch, "E36.visualSharp", {"position": v(75.45, 129.74) * mm});
            skArc(sketch, "E36.filletArc", {"start": v(75.45, 131.53) * mm, "mid": v(75.99, 130.38) * mm, "end": v(77.21, 130.05) * mm});
            skCircle(sketch, "E37", {"center": v(80, 173.52) * mm, "radius": 1 * mm});
            skCircle(sketch, "E38", {"center": v(80, 126.48) * mm, "radius": 1 * mm});
            skLineSegment(sketch, "E39", {"start": v(75.98, 150) * mm, "end": v(76.95, 150) * mm, "construction": true});
            skSolve(sketch);
        }
        {
            var Q0;
            Q0=qSketchRegion(id+"F0",true);
            extrude(context, id + "F1", {"entities" : qUnion([Q0]), "depth" : 4 * mm});
        }
        {
            var Q0;
            Q0=makeQuery(id+"F1.opExtrude","CAP_FACE",FACE,{"disambiguationData":[OSD([sQuery(id+"F0.wireOp",EDGE,"E0.bottom"),sQuery(id+"F0.wireOp",EDGE,"E0.top"),sQuery(id+"F0.wireOp",EDGE,"E0.left"),sQuery(id+"F0.wireOp",EDGE,"E0.right"),sQuery(id+"F0.wireOp",EDGE,"E1"),sQuery(id+"F0.wireOp",EDGE,"E2"),sQuery(id+"F0.wireOp",EDGE,"E3"),sQuery(id+"F0.wireOp",EDGE,"E5.trimOffspring"),sQuery(id+"F0.wireOp",EDGE,"E6.0.1.0"),sQuery(id+"F0.wireOp",EDGE,"E6.0.1.1"),sQuery(id+"F0.wireOp",EDGE,"E6.0.1.2"),sQuery(id+"F0.wireOp",EDGE,"E6.0.1.4"),sQuery(id+"F0.wireOp",EDGE,"E7.0.1.0"),sQuery(id+"F0.wireOp",EDGE,"E7.3.1.0"),sQuery(id+"F0.wireOp",EDGE,"E7.6.1.0"),sQuery(id+"F0.wireOp",EDGE,"E7.13.1.0"),sQuery(id+"F0.wireOp",EDGE,"E7.0.1.1"),sQuery(id+"F0.wireOp",EDGE,"E7.3.1.1"),sQuery(id+"F0.wireOp",EDGE,"E7.6.1.1"),sQuery(id+"F0.wireOp",EDGE,"E7.13.1.1"),sQuery(id+"F0.wireOp",EDGE,"E7.0.2.0"),sQuery(id+"F0.wireOp",EDGE,"E7.3.2.0"),sQuery(id+"F0.wireOp",EDGE,"E7.6.2.0"),sQuery(id+"F0.wireOp",EDGE,"E7.13.2.0"),sQuery(id+"F0.wireOp",EDGE,"E7.0.2.1"),sQuery(id+"F0.wireOp",EDGE,"E7.3.2.1"),sQuery(id+"F0.wireOp",EDGE,"E7.6.2.1"),sQuery(id+"F0.wireOp",EDGE,"E7.13.2.1"),sQuery(id+"F0.wireOp",EDGE,"E7.0.3.0"),sQuery(id+"F0.wireOp",EDGE,"E7.3.3.0"),sQuery(id+"F0.wireOp",EDGE,"E7.6.3.0"),sQuery(id+"F0.wireOp",EDGE,"E7.13.3.0"),sQuery(id+"F0.wireOp",EDGE,"E7.0.3.1"),sQuery(id+"F0.wireOp",EDGE,"E7.3.3.1"),sQuery(id+"F0.wireOp",EDGE,"E7.6.3.1"),sQuery(id+"F0.wireOp",EDGE,"E7.13.3.1"),sQuery(id+"F0.wireOp",EDGE,"E7.0.4.0"),sQuery(id+"F0.wireOp",EDGE,"E7.3.4.0"),sQuery(id+"F0.wireOp",EDGE,"E7.6.4.0"),sQuery(id+"F0.wireOp",EDGE,"E7.13.4.0"),sQuery(id+"F0.wireOp",EDGE,"E7.0.4.1"),sQuery(id+"F0.wireOp",EDGE,"E7.3.4.1"),sQuery(id+"F0.wireOp",EDGE,"E7.6.4.1"),sQuery(id+"F0.wireOp",EDGE,"E7.13.4.1"),sQuery(id+"F0.wireOp",EDGE,"E9"),sQuery(id+"F0.wireOp",EDGE,"E10"),sQuery(id+"F0.wireOp",EDGE,"E11"),sQuery(id+"F0.wireOp",EDGE,"E13.trimOffspring"),sQuery(id+"F0.wireOp",EDGE,"E14"),sQuery(id+"F0.wireOp",EDGE,"E15"),sQuery(id+"F0.wireOp",EDGE,"E16"),sQuery(id+"F0.wireOp",EDGE,"E17"),sQuery(id+"F0.wireOp",EDGE,"E19.filletArc"),sQuery(id+"F0.wireOp",EDGE,"E20.filletArc"),sQuery(id+"F0.wireOp",EDGE,"E21.filletArc"),sQuery(id+"F0.wireOp",EDGE,"E22.filletArc"),sQuery(id+"F0.wireOp",EDGE,"E23"),sQuery(id+"F0.wireOp",EDGE,"E24"),sQuery(id+"F0.wireOp",EDGE,"E26.0.1.6"),sQuery(id+"F0.wireOp",EDGE,"E26.0.1.7"),sQuery(id+"F0.wireOp",EDGE,"E26.0.1.8"),sQuery(id+"F0.wireOp",EDGE,"E26.0.1.9"),sQuery(id+"F0.wireOp",EDGE,"E26.0.1.10"),sQuery(id+"F0.wireOp",EDGE,"E26.0.1.11"),sQuery(id+"F0.wireOp",EDGE,"E26.0.1.12"),sQuery(id+"F0.wireOp",EDGE,"E26.0.1.13"),sQuery(id+"F0.wireOp",EDGE,"E26.0.1.14"),sQuery(id+"F0.wireOp",EDGE,"E26.0.1.15"),sQuery(id+"F0.wireOp",EDGE,"E26.1.0.6"),sQuery(id+"F0.wireOp",EDGE,"E26.1.0.7"),sQuery(id+"F0.wireOp",EDGE,"E26.1.0.8"),sQuery(id+"F0.wireOp",EDGE,"E26.1.0.9"),sQuery(id+"F0.wireOp",EDGE,"E26.1.0.10"),sQuery(id+"F0.wireOp",EDGE,"E26.1.0.11"),sQuery(id+"F0.wireOp",EDGE,"E26.1.0.12"),sQuery(id+"F0.wireOp",EDGE,"E26.1.0.13"),sQuery(id+"F0.wireOp",EDGE,"E26.1.0.14"),sQuery(id+"F0.wireOp",EDGE,"E26.1.0.15"),sQuery(id+"F0.wireOp",EDGE,"E26.1.1.6"),sQuery(id+"F0.wireOp",EDGE,"E26.1.1.7"),sQuery(id+"F0.wireOp",EDGE,"E26.1.1.8"),sQuery(id+"F0.wireOp",EDGE,"E26.1.1.9"),sQuery(id+"F0.wireOp",EDGE,"E26.1.1.10"),sQuery(id+"F0.wireOp",EDGE,"E26.1.1.11"),sQuery(id+"F0.wireOp",EDGE,"E26.1.1.12"),sQuery(id+"F0.wireOp",EDGE,"E26.1.1.13"),sQuery(id+"F0.wireOp",EDGE,"E26.1.1.14"),sQuery(id+"F0.wireOp",EDGE,"E26.1.1.15"),sQuery(id+"F0.wireOp",EDGE,"E26.2.0.6"),sQuery(id+"F0.wireOp",EDGE,"E26.2.0.7"),sQuery(id+"F0.wireOp",EDGE,"E26.2.0.8"),sQuery(id+"F0.wireOp",EDGE,"E26.2.0.9"),sQuery(id+"F0.wireOp",EDGE,"E26.2.0.10"),sQuery(id+"F0.wireOp",EDGE,"E26.2.0.11"),sQuery(id+"F0.wireOp",EDGE,"E26.2.0.12"),sQuery(id+"F0.wireOp",EDGE,"E26.2.0.13"),sQuery(id+"F0.wireOp",EDGE,"E26.2.0.14"),sQuery(id+"F0.wireOp",EDGE,"E26.2.0.15"),sQuery(id+"F0.wireOp",EDGE,"E26.2.1.6"),sQuery(id+"F0.wireOp",EDGE,"E26.2.1.7"),sQuery(id+"F0.wireOp",EDGE,"E26.2.1.8"),sQuery(id+"F0.wireOp",EDGE,"E26.2.1.9"),sQuery(id+"F0.wireOp",EDGE,"E26.2.1.10"),sQuery(id+"F0.wireOp",EDGE,"E26.2.1.11"),sQuery(id+"F0.wireOp",EDGE,"E26.2.1.12"),sQuery(id+"F0.wireOp",EDGE,"E26.2.1.13"),sQuery(id+"F0.wireOp",EDGE,"E26.2.1.14"),sQuery(id+"F0.wireOp",EDGE,"E26.2.1.15"),sQuery(id+"F0.wireOp",EDGE,"E26.3.0.6"),sQuery(id+"F0.wireOp",EDGE,"E26.3.0.7"),sQuery(id+"F0.wireOp",EDGE,"E26.3.0.8"),sQuery(id+"F0.wireOp",EDGE,"E26.3.0.9"),sQuery(id+"F0.wireOp",EDGE,"E26.3.0.10"),sQuery(id+"F0.wireOp",EDGE,"E26.3.0.11"),sQuery(id+"F0.wireOp",EDGE,"E26.3.0.12"),sQuery(id+"F0.wireOp",EDGE,"E26.3.0.13"),sQuery(id+"F0.wireOp",EDGE,"E26.3.0.14"),sQuery(id+"F0.wireOp",EDGE,"E26.3.0.15"),sQuery(id+"F0.wireOp",EDGE,"E26.3.1.6"),sQuery(id+"F0.wireOp",EDGE,"E26.3.1.7"),sQuery(id+"F0.wireOp",EDGE,"E26.3.1.8"),sQuery(id+"F0.wireOp",EDGE,"E26.3.1.9"),sQuery(id+"F0.wireOp",EDGE,"E26.3.1.10"),sQuery(id+"F0.wireOp",EDGE,"E26.3.1.11"),sQuery(id+"F0.wireOp",EDGE,"E26.3.1.12"),sQuery(id+"F0.wireOp",EDGE,"E26.3.1.13"),sQuery(id+"F0.wireOp",EDGE,"E26.3.1.14"),sQuery(id+"F0.wireOp",EDGE,"E26.3.1.15"),sQuery(id+"F0.wireOp",EDGE,"E26.4.0.6"),sQuery(id+"F0.wireOp",EDGE,"E26.4.0.7"),sQuery(id+"F0.wireOp",EDGE,"E26.4.0.8"),sQuery(id+"F0.wireOp",EDGE,"E26.4.0.9"),sQuery(id+"F0.wireOp",EDGE,"E26.4.0.10"),sQuery(id+"F0.wireOp",EDGE,"E26.4.0.11"),sQuery(id+"F0.wireOp",EDGE,"E26.4.0.12"),sQuery(id+"F0.wireOp",EDGE,"E26.4.0.13"),sQuery(id+"F0.wireOp",EDGE,"E26.4.0.14"),sQuery(id+"F0.wireOp",EDGE,"E26.4.0.15"),sQuery(id+"F0.wireOp",EDGE,"E26.4.1.6"),sQuery(id+"F0.wireOp",EDGE,"E26.4.1.7"),sQuery(id+"F0.wireOp",EDGE,"E26.4.1.8"),sQuery(id+"F0.wireOp",EDGE,"E26.4.1.9"),sQuery(id+"F0.wireOp",EDGE,"E26.4.1.10"),sQuery(id+"F0.wireOp",EDGE,"E26.4.1.11"),sQuery(id+"F0.wireOp",EDGE,"E26.4.1.12"),sQuery(id+"F0.wireOp",EDGE,"E26.4.1.13"),sQuery(id+"F0.wireOp",EDGE,"E26.4.1.14"),sQuery(id+"F0.wireOp",EDGE,"E26.4.1.15"),sQuery(id+"F0.wireOp",EDGE,"E27.0.1.1"),sQuery(id+"F0.wireOp",EDGE,"E27.0.1.2"),sQuery(id+"F0.wireOp",EDGE,"E27.0.1.3"),sQuery(id+"F0.wireOp",EDGE,"E27.0.1.4"),sQuery(id+"F0.wireOp",EDGE,"E27.1.0.1"),sQuery(id+"F0.wireOp",EDGE,"E27.1.0.2"),sQuery(id+"F0.wireOp",EDGE,"E27.1.0.3"),sQuery(id+"F0.wireOp",EDGE,"E27.1.0.4"),sQuery(id+"F0.wireOp",EDGE,"E27.1.1.1"),sQuery(id+"F0.wireOp",EDGE,"E27.1.1.2"),sQuery(id+"F0.wireOp",EDGE,"E27.1.1.3"),sQuery(id+"F0.wireOp",EDGE,"E27.1.1.4"),sQuery(id+"F0.wireOp",EDGE,"E27.2.0.1"),sQuery(id+"F0.wireOp",EDGE,"E27.2.0.2"),sQuery(id+"F0.wireOp",EDGE,"E27.2.0.3"),sQuery(id+"F0.wireOp",EDGE,"E27.2.0.4"),sQuery(id+"F0.wireOp",EDGE,"E27.2.1.1"),sQuery(id+"F0.wireOp",EDGE,"E27.2.1.2"),sQuery(id+"F0.wireOp",EDGE,"E27.2.1.3"),sQuery(id+"F0.wireOp",EDGE,"E27.2.1.4"),sQuery(id+"F0.wireOp",EDGE,"E27.3.0.1"),sQuery(id+"F0.wireOp",EDGE,"E27.3.0.2"),sQuery(id+"F0.wireOp",EDGE,"E27.3.0.3"),sQuery(id+"F0.wireOp",EDGE,"E27.3.0.4"),sQuery(id+"F0.wireOp",EDGE,"E27.3.1.1"),sQuery(id+"F0.wireOp",EDGE,"E27.3.1.2"),sQuery(id+"F0.wireOp",EDGE,"E27.3.1.3"),sQuery(id+"F0.wireOp",EDGE,"E27.3.1.4"),sQuery(id+"F0.wireOp",EDGE,"E27.4.0.1"),sQuery(id+"F0.wireOp",EDGE,"E27.4.0.2"),sQuery(id+"F0.wireOp",EDGE,"E27.4.0.3"),sQuery(id+"F0.wireOp",EDGE,"E27.4.0.4"),sQuery(id+"F0.wireOp",EDGE,"E27.4.1.1"),sQuery(id+"F0.wireOp",EDGE,"E27.4.1.2"),sQuery(id+"F0.wireOp",EDGE,"E27.4.1.3"),sQuery(id+"F0.wireOp",EDGE,"E27.4.1.4")])],"isStart":false});
            var sketch = newSketch(context, id + "F2", { "sketchPlane" : qUnion([Q0])});
            skLineSegment(sketch, "E40.0", {"start": v(-105, 185) * mm, "end": v(105, 185) * mm});
            skLineSegment(sketch, "E41.0", {"start": v(105, 185) * mm, "end": v(105, -185) * mm});
            skLineSegment(sketch, "E42.0", {"start": v(-105, 185) * mm, "end": v(-105, -185) * mm});
            skLineSegment(sketch, "E43.0", {"start": v(-105, -185) * mm, "end": v(105, -185) * mm});
            skLineSegment(sketch, "E44.0", {"start": v(-120, 200) * mm, "end": v(120, 200) * mm});
            skLineSegment(sketch, "E45.0", {"start": v(-120, -200) * mm, "end": v(-120, 200) * mm});
            skLineSegment(sketch, "E46.0", {"start": v(120, -200) * mm, "end": v(120, 200) * mm});
            skLineSegment(sketch, "E47.0", {"start": v(-120, -200) * mm, "end": v(120, -200) * mm});
            skSolve(sketch);
        }
        {
            var Q0;
            Q0=makeQuery(id+"F2.imprint","IMPRINT",FACE,{"disambiguationData":[TD([[makeQuery(id+"F2.imprint","IMPRINT",EDGE,{"derivedFrom":sQuery(id+"F2.wireOp",EDGE,"E40.0")}),1.0]])]});
            extrude(context, id + "F3", {"entities" : qUnion([Q0]), "operationType" : NewBodyOperationType.REMOVE, "oppositeDirection" : true, "depth" : 1.5 * mm});
        }
        {
            var Q0;
            Q0=qCreatedBy(makeId("Top.planeOp"),FACE);
            var sketch = newSketch(context, id + "F4", { "sketchPlane" : qUnion([Q0])});
            skLineSegment(sketch, "E48.bottom", {"start": v(-120, 310) * mm, "end": v(85, 310) * mm});
            skLineSegment(sketch, "E48.top", {"start": v(-120, 210) * mm, "end": v(85, 210) * mm});
            skLineSegment(sketch, "E48.left", {"start": v(-120, 310) * mm, "end": v(-120, 210) * mm});
            skLineSegment(sketch, "E48.right", {"start": v(85, 310) * mm, "end": v(85, 210) * mm});
            skLineSegment(sketch, "E49", {"start": v(-84.93, 267.53) * mm, "end": v(-84.93, 252.47) * mm});
            skLineSegment(sketch, "E50", {"start": v(-82.58, 250.5) * mm, "end": v(-76.73, 251.53) * mm});
            skLineSegment(sketch, "E51", {"start": v(-75.08, 253.5) * mm, "end": v(-75.08, 266.5) * mm});
            skLineSegment(sketch, "E52", {"start": v(-76.73, 268.47) * mm, "end": v(-82.58, 269.5) * mm});
            skLineSegment(sketch, "E53", {"start": v(-80, 269.05) * mm, "end": v(-80, 250.95) * mm, "construction": true});
            skLineSegment(sketch, "E54", {"start": v(-84.92, 260) * mm, "end": v(-75.08, 260) * mm, "construction": true});
            skCircle(sketch, "E55", {"center": v(-80, 272.5) * mm, "radius": 1 * mm});
            skCircle(sketch, "E56", {"center": v(-80, 247.5) * mm, "radius": 1 * mm});
            skPoint(sketch, "E57.visualSharp", {"position": v(-84.92, 269.91) * mm});
            skArc(sketch, "E57.filletArc", {"start": v(-82.58, 269.5) * mm, "mid": v(-84.21, 269.06) * mm, "end": v(-84.92, 267.53) * mm});
            skPoint(sketch, "E58.visualSharp", {"position": v(-84.92, 250.09) * mm});
            skArc(sketch, "E58.filletArc", {"start": v(-84.92, 252.47) * mm, "mid": v(-84.21, 250.94) * mm, "end": v(-82.58, 250.5) * mm});
            skPoint(sketch, "E59.visualSharp", {"position": v(-75.07, 251.82) * mm});
            skArc(sketch, "E59.filletArc", {"start": v(-76.73, 251.53) * mm, "mid": v(-75.54, 252.22) * mm, "end": v(-75.08, 253.5) * mm});
            skPoint(sketch, "E60.visualSharp", {"position": v(-75.07, 268.18) * mm});
            skArc(sketch, "E60.filletArc", {"start": v(-75.08, 266.5) * mm, "mid": v(-75.54, 267.78) * mm, "end": v(-76.73, 268.47) * mm});
            skLineSegment(sketch, "E61.bottom", {"start": v(-45.5, 271.5) * mm, "end": v(-14.5, 271.5) * mm});
            skLineSegment(sketch, "E61.top", {"start": v(-45.5, 248.5) * mm, "end": v(-14.5, 248.5) * mm});
            skLineSegment(sketch, "E61.left", {"start": v(-45.5, 271.5) * mm, "end": v(-45.5, 248.5) * mm});
            skLineSegment(sketch, "E61.right", {"start": v(-14.5, 271.5) * mm, "end": v(-14.5, 248.5) * mm});
            skLineSegment(sketch, "E62", {"start": v(-45.5, 260) * mm, "end": v(-14.5, 260) * mm, "construction": true});
            skCircle(sketch, "E63", {"center": v(-10, 260) * mm, "radius": 1.65 * mm});
            skLineSegment(sketch, "E64", {"start": v(-30, 271.5) * mm, "end": v(-30, 248.5) * mm, "construction": true});
            skCircle(sketch, "E65", {"center": v(-50, 260) * mm, "radius": 1.65 * mm});
            skLineSegment(sketch, "E66.bottom", {"start": v(13.85, 282) * mm, "end": v(56.15, 282) * mm});
            skLineSegment(sketch, "E66.top", {"start": v(13.85, 238) * mm, "end": v(56.15, 238) * mm});
            skLineSegment(sketch, "E66.left", {"start": v(13.85, 282) * mm, "end": v(13.85, 238) * mm});
            skLineSegment(sketch, "E66.right", {"start": v(56.15, 282) * mm, "end": v(56.15, 238) * mm});
            skLineSegment(sketch, "E67.bottom", {"start": v(13.85, 260) * mm, "end": v(56.15, 260) * mm, "construction": true});
            skLineSegment(sketch, "E67.top", {"start": v(13.85, 260) * mm, "end": v(56.15, 260) * mm, "construction": true});
            skLineSegment(sketch, "E67.left", {"start": v(13.85, 260) * mm, "end": v(13.85, 260) * mm});
            skLineSegment(sketch, "E67.right", {"start": v(56.15, 260) * mm, "end": v(56.15, 260) * mm});
            skLineSegment(sketch, "E68", {"start": v(35, 282) * mm, "end": v(35, 238) * mm, "construction": true});
            skSolve(sketch);
        }
        {
            var Q0;
            Q0=qSketchRegion(id+"F4",true);
            extrude(context, id + "F5", {"entities" : qUnion([Q0]), "depth" : 4 * mm});
        }
        {
            var Q0;
            Q0=makeQuery(id+"F5.opExtrude","CAP_FACE",FACE,{"disambiguationData":[OSD([sQuery(id+"F4.wireOp",EDGE,"E48.bottom"),sQuery(id+"F4.wireOp",EDGE,"E48.top"),sQuery(id+"F4.wireOp",EDGE,"E48.left"),sQuery(id+"F4.wireOp",EDGE,"E48.right"),sQuery(id+"F4.wireOp",EDGE,"E49"),sQuery(id+"F4.wireOp",EDGE,"E50"),sQuery(id+"F4.wireOp",EDGE,"E51"),sQuery(id+"F4.wireOp",EDGE,"E52"),sQuery(id+"F4.wireOp",EDGE,"E55"),sQuery(id+"F4.wireOp",EDGE,"E56"),sQuery(id+"F4.wireOp",EDGE,"E57.filletArc"),sQuery(id+"F4.wireOp",EDGE,"E58.filletArc"),sQuery(id+"F4.wireOp",EDGE,"E59.filletArc"),sQuery(id+"F4.wireOp",EDGE,"E60.filletArc"),sQuery(id+"F4.wireOp",EDGE,"E61.bottom"),sQuery(id+"F4.wireOp",EDGE,"E61.top"),sQuery(id+"F4.wireOp",EDGE,"E61.left"),sQuery(id+"F4.wireOp",EDGE,"E61.right"),sQuery(id+"F4.wireOp",EDGE,"E63"),sQuery(id+"F4.wireOp",EDGE,"E65"),sQuery(id+"F4.wireOp",EDGE,"E66.bottom"),sQuery(id+"F4.wireOp",EDGE,"E66.top"),sQuery(id+"F4.wireOp",EDGE,"E66.left"),sQuery(id+"F4.wireOp",EDGE,"E66.right")])],"isStart":false});
            var sketch = newSketch(context, id + "F6", { "sketchPlane" : qUnion([Q0])});
            skLineSegment(sketch, "E69.bottom", {"start": v(-105, 295) * mm, "end": v(70, 295) * mm});
            skLineSegment(sketch, "E69.top", {"start": v(-105, 225) * mm, "end": v(70, 225) * mm});
            skLineSegment(sketch, "E69.left", {"start": v(-105, 295) * mm, "end": v(-105, 225) * mm});
            skLineSegment(sketch, "E69.right", {"start": v(70, 295) * mm, "end": v(70, 225) * mm});
            skLineSegment(sketch, "E70.0", {"start": v(-120, 310) * mm, "end": v(85, 310) * mm});
            skLineSegment(sketch, "E71.0", {"start": v(-120, 310) * mm, "end": v(-120, 210) * mm});
            skLineSegment(sketch, "E72.0", {"start": v(-120, 210) * mm, "end": v(85, 210) * mm});
            skLineSegment(sketch, "E73.0", {"start": v(85, 310) * mm, "end": v(85, 210) * mm});
            skSolve(sketch);
        }
        {
            var Q0;
            Q0=qSketchRegion(id+"F6",true);
            extrude(context, id + "F7", {"entities" : qUnion([Q0]), "operationType" : NewBodyOperationType.REMOVE, "oppositeDirection" : true, "depth" : 1.5 * mm});
        }
    });
